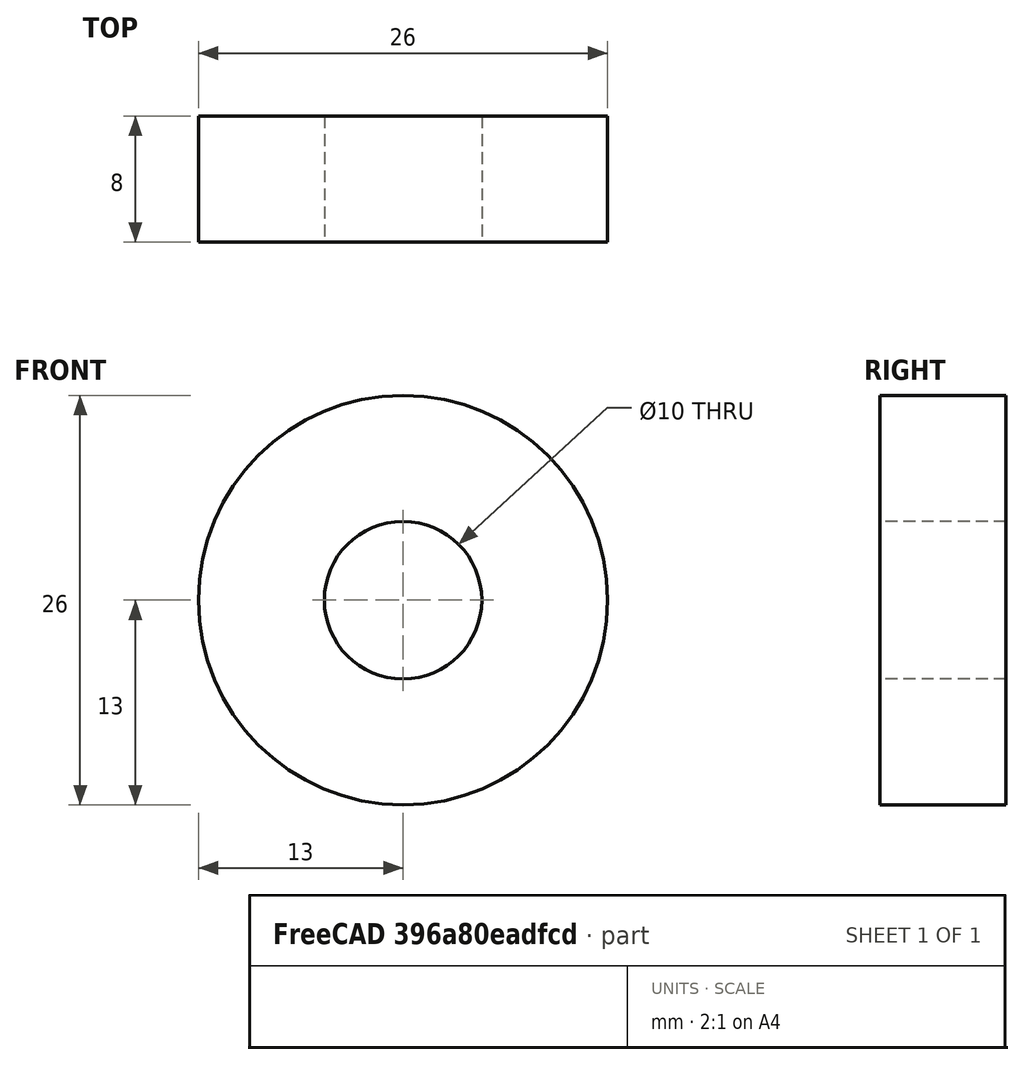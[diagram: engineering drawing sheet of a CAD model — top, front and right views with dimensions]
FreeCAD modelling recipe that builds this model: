
FCSTD DOCUMENT  (FreeCAD 0.21R33668 +7 (Git))
Label: 6000
License: All rights reserved
LicenseURL: https://en.wikipedia.org/wiki/All_rights_reserved
objects: Sketcher::SketchObject×1, PartDesign::Revolution×1, PartDesign::Body×1
note: 4 computed .brp shape members not serialized (recipe doc carries the construction recipe); baked Part::Feature solids carry a one-line shape summary decoded from their .brp

FEATURE [Sketcher::SketchObject] Sketch
  FullyConstrained = true
  MapMode = 5
  Placement = pos=(0,0,0) rot=(0.57735,0.57735,0.57735;2.0944rad)
  Support = -> [YZ_Plane]
  sketch-geometry (4):
    g0: LineSegment StartX=-4 StartY=13 StartZ=0 EndX=4 EndY=13 EndZ=0
    g1: LineSegment StartX=4 StartY=13 StartZ=0 EndX=4 EndY=5 EndZ=0
    g2: LineSegment StartX=4 StartY=5 StartZ=0 EndX=-4 EndY=5 EndZ=0
    g3: LineSegment StartX=-4 StartY=5 StartZ=0 EndX=-4 EndY=13 EndZ=0
  constraints (11):
    c: Coincident(g0,g1)
    c: Coincident(g1,g2)
    c: Coincident(g2,g3)
    c: Coincident(g3,g0)
    c: Horizontal(g2)
    c: Vertical(g1)
    c: Vertical(g3)
    c: Symmetric(g0,g0,g-2)
    c: DistanceY(g-1,g1) = 5
    c: DistanceY(g-1,g0) = 13
    c: DistanceX(g0,g0) = 8
FEATURE [PartDesign::Revolution] Revolution
  Angle = 360
  Axis = (3e-16,1,-2e-16)
  Base = (0,0,0)
  Placement = pos=(0,0,0) rot=(1,1,1;2.0944rad)
  Profile = -> Sketch
  ReferenceAxis = -> Sketch [H_Axis]
FEATURE [PartDesign::Body] Body  label="6000"
  Group = -> [Sketch,Revolution]
  Origin = -> Origin
  Tip = -> Revolution
